FCSTD DOCUMENT  (FreeCAD 1.1R20260325 (Git shallow))
Label: align_image_test_1
License: All rights reserved
LicenseURL: https://en.wikipedia.org/wiki/All_rights_reserved
objects: Sketcher::SketchObject×2, App::FeaturePython×2, Image::ImagePlane×1
note: 4 computed .brp shape members not serialized (recipe doc carries the construction recipe); baked Part::Feature solids carry a one-line shape summary decoded from their .brp

FEATURE [Image::ImagePlane] IMG_20260619_210034_279
  Placement = pos=(959,0,0) rot=(0,0,1;1.5708rad)
  XSize = 1083.6
  YSize = 609.524
FEATURE [Sketcher::SketchObject] CalibSketch
  ArcFitTolerance = 1e-06
  ExternalTypes = [0]
  FullyConstrained = false
  MakeInternals = false
  _ExternalGeoVersion = 1
  sketch-geometry (4):
    g0: LineSegment StartX=794.508 StartY=-435.468 StartZ=0 EndX=1147.87 EndY=-435.468 EndZ=0
    g1: LineSegment StartX=1147.87 StartY=-435.468 StartZ=0 EndX=1147.87 EndY=515.292 EndZ=0
    g2: LineSegment StartX=1147.87 StartY=515.292 StartZ=0 EndX=847.406 EndY=540.108 EndZ=0
    g3: LineSegment StartX=847.406 StartY=540.108 StartZ=0 EndX=794.508 EndY=-435.468 EndZ=0
  constraints (4):
    c: Coincident(g0,g1)
    c: Coincident(g1,g2)
    c: Coincident(g2,g3)
    c: Coincident(g3,g0)
FEATURE [App::FeaturePython] IMG_20260619_210034_279_aligned  label="IMG_20260619_210034_279_aligned003"  # WARN: FeaturePython — macro-defined, semantics opaque (R4)
  Corner0 = (1263.76,-541.799,0)
  Corner1 = (654.238,541.799,0)
  CornerX = (1263.76,541.799,0)
  CornerY = (654.238,-541.799,0)
  ImageFile = <userpath>/.cache/FreeCAD/Cache/FreeCAD_Doc_cc8e9ee5-b53c-482f-9fe8-e2ddf17d9c98_9d2ae5_603203/IMG_20260619_210034_279.jpg
  SourceImage = -> IMG_20260619_210034_279
FEATURE [Sketcher::SketchObject] CalibSketch_aligned
  ArcFitTolerance = 1e-06
  ExternalTypes = [0]
  FullyConstrained = false
  MakeInternals = false
  _ExternalGeoVersion = 1
  sketch-geometry (4):
    g0: LineSegment StartX=-400 StartY=6.59e-12 StartZ=0 EndX=-8.2991e-12 EndY=3.06442e-11 EndZ=0
    g1: LineSegment StartX=-8.3224e-12 StartY=3.06442e-11 StartZ=0 EndX=5.08293e-11 EndY=1200 EndZ=0
    g2: LineSegment StartX=5.08293e-11 StartY=1200 StartZ=0 EndX=-400 EndY=1200 EndZ=0
    g3: LineSegment StartX=-400 StartY=1200 StartZ=0 EndX=-400 EndY=6.5938e-12 EndZ=0
FEATURE [App::FeaturePython] ImageCalibration  label="ImageCalibration002"  # WARN: FeaturePython — macro-defined, semantics opaque (R4)
  AlignedSketch = -> CalibSketch_aligned
  Constraints = {\n  "lengths": [\n    {\n      "line": 0,\n      "target_mm": 400.0\n    },\n    {\n      "line": 1,\n      "target_mm": 1200.0\n    }\n  ],\n  "parallel": [],\n  "perpendicular": [],\n  "horizontal": [\n    {\n      "line": 0\n    },\n    {\n      "line": 2\n    }\n  ],\n  "vertical": [\n    {\n      "line": 1\n    },\n    {\n      "line": 3\n    }\n  ],\n  "fixed_points": [\n    {\n      "point": 0,\n      "target_x_mm": 0.0,\n      "target_y_mm": 0.0\n    }\n  ]\n}
  Image = -> IMG_20260619_210034_279
  Lines = [\n  {\n    "line": 0,\n    "u0": 0.09812767578123717,\n    "v0": 0.7698696874998565,\n    "u1": 0.09812767578120896,\n    "v1": 0.1901351562500289\n  },\n  {\n    "line": 1,\n    "u0": 0.09812767578120896,\n    "v0": 0.1901351562500289,\n    "u1": 0.975538188842763,\n    "v1": 0.19013515624983887\n  },\n  {\n    "line": 2,\n    "u0": 0.975538188842763,\n    "v0": 0.19013515624983887,\n    "u1": 0.9984395117187885,\n    "v1": 0.6830839062499384\n  },\n  {\n    "line": 3,\n    "u0": 0.9984395117187885,\n    "v0": 0.6830839062499384,\n    "u1": 0.09812767578123717,\n    "v1": 0.7698696874998565\n  }\n]
  Points = [\n  {\n    "point": 0,\n    "u": 0.09812767578120896,\n    "v": 0.1901351562500289\n  },\n  {\n    "point": 1,\n    "u": 0.09812767578123717,\n    "v": 0.7698696874998565\n  },\n  {\n    "point": 2,\n    "u": 0.975538188842763,\n    "v": 0.19013515624983887\n  },\n  {\n    "point": 3,\n    "u": 0.9984395117187885,\n    "v": 0.6830839062499384\n  }\n]
  Sketch = -> CalibSketch
